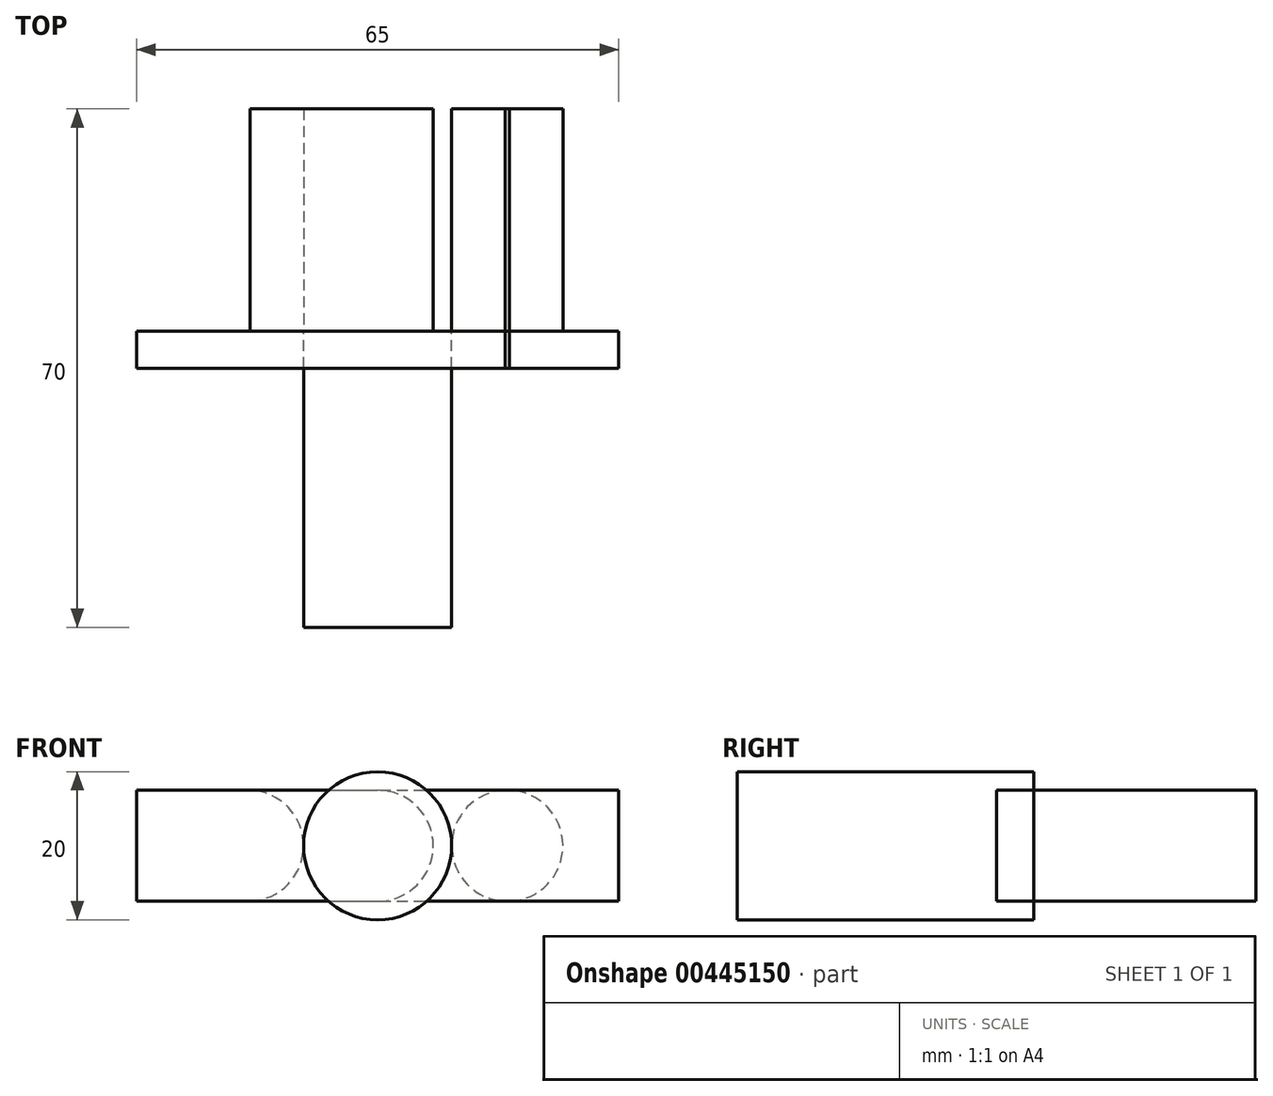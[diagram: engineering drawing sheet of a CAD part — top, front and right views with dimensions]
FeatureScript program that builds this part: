
annotation { "Feature Type Name" : "Feature", "Feature Type Description" : "" }
export const myFeature = defineFeature(function(context is Context, id is Id, definition is map)
    precondition{}
    {
        {
            var Q0;
            Q0=qCreatedBy(makeId("Front.planeOp"),FACE);
            var sketch = newSketch(context, id + "F0", { "sketchPlane" : qUnion([Q0])});
            skLineSegment(sketch, "E0.bottom", {"start": v(-32.5, 7.5) * mm, "end": v(32.5, 7.5) * mm});
            skLineSegment(sketch, "E0.top", {"start": v(-32.5, -7.5) * mm, "end": v(32.5, -7.5) * mm});
            skLineSegment(sketch, "E0.left", {"start": v(-32.5, 7.5) * mm, "end": v(-32.5, -7.5) * mm});
            skLineSegment(sketch, "E0.right", {"start": v(32.5, 7.5) * mm, "end": v(32.5, -7.5) * mm});
            skPoint(sketch, "E0.middle", {"position": v(0, 0) * mm});
            skCircle(sketch, "E1", {"center": v(0, 0) * mm, "radius": 7.5 * mm});
            skCircle(sketch, "E2", {"center": v(-17.5, 0) * mm, "radius": 7.5 * mm});
            skCircle(sketch, "E3", {"center": v(17.5, 0) * mm, "radius": 7.5 * mm});
            skSolve(sketch);
        }
        {
            var Q0;
            {var subQ0=sQuery(id+"F0.wireOp",EDGE,"E0.left");Q0=makeQuery(id+"F0.imprint","IMPRINT",FACE,{"disambiguationData":[TD([[makeQuery(id+"F0.imprint","IMPRINT",EDGE,{"derivedFrom":subQ0}),1.0]])]});}
            var Q1;
            {var subQ0=sQuery(id+"F0.wireOp",EDGE,"E2");var subQ1=sQuery(id+"F0.wireOp",EDGE,"E0.bottom");var subQ2=makeQuery(id+"F0.imprint","INTERSECT",VERTEX,{"disambiguationData":[OD(1.0)],"derivedFrom":[subQ1,subQ0]});Q1=makeQuery(id+"F0.imprint","IMPRINT",FACE,{"disambiguationData":[TD([[makeQuery(id+"F0.imprint","IMPRINT",EDGE,{"disambiguationData":[TD([[subQ2,-1.0]])],"derivedFrom":subQ1}),-1.0]])]});}
            var Q2;
            {var subQ0=sQuery(id+"F0.wireOp",EDGE,"E1");var subQ1=sQuery(id+"F0.wireOp",EDGE,"E0.bottom");var subQ2=makeQuery(id+"F0.imprint","INTERSECT",VERTEX,{"derivedFrom":[subQ1,subQ0]});Q2=makeQuery(id+"F0.imprint","IMPRINT",FACE,{"disambiguationData":[TD([[makeQuery(id+"F0.imprint","IMPRINT",EDGE,{"disambiguationData":[TD([[subQ2,-1.0]])],"derivedFrom":subQ1}),-1.0]])]});}
            var Q3;
            {var subQ0=sQuery(id+"F0.wireOp",EDGE,"E0.right");Q3=makeQuery(id+"F0.imprint","IMPRINT",FACE,{"disambiguationData":[TD([[makeQuery(id+"F0.imprint","IMPRINT",EDGE,{"derivedFrom":subQ0}),-1.0]])]});}
            var Q4;
            {var subQ0=sQuery(id+"F0.wireOp",EDGE,"E3");var subQ1=sQuery(id+"F0.wireOp",EDGE,"E0.top");var subQ2=makeQuery(id+"F0.imprint","INTERSECT",VERTEX,{"disambiguationData":[OD(0.0)],"derivedFrom":[subQ1,subQ0]});Q4=makeQuery(id+"F0.imprint","IMPRINT",FACE,{"disambiguationData":[TD([[makeQuery(id+"F0.imprint","IMPRINT",EDGE,{"disambiguationData":[TD([[subQ2,-1.0]])],"derivedFrom":subQ1}),-1.0]])]});}
            var Q5;
            {var subQ0=sQuery(id+"F0.wireOp",EDGE,"E3");var subQ1=sQuery(id+"F0.wireOp",EDGE,"E0.bottom");var subQ2=makeQuery(id+"F0.imprint","INTERSECT",VERTEX,{"disambiguationData":[OD(0.0)],"derivedFrom":[subQ1,subQ0]});Q5=makeQuery(id+"F0.imprint","IMPRINT",FACE,{"disambiguationData":[TD([[makeQuery(id+"F0.imprint","IMPRINT",EDGE,{"disambiguationData":[TD([[subQ2,-1.0]])],"derivedFrom":subQ1}),1.0]])]});}
            var Q6;
            {var subQ0=sQuery(id+"F0.wireOp",EDGE,"E2");var subQ1=sQuery(id+"F0.wireOp",EDGE,"E0.bottom");var subQ2=makeQuery(id+"F0.imprint","INTERSECT",VERTEX,{"disambiguationData":[OD(0.0)],"derivedFrom":[subQ1,subQ0]});Q6=makeQuery(id+"F0.imprint","IMPRINT",FACE,{"disambiguationData":[TD([[makeQuery(id+"F0.imprint","IMPRINT",EDGE,{"disambiguationData":[TD([[subQ2,-1.0]])],"derivedFrom":subQ1}),1.0]])]});}
            var Q7;
            {var subQ0=sQuery(id+"F0.wireOp",EDGE,"E2");var subQ1=sQuery(id+"F0.wireOp",EDGE,"E0.top");var subQ2=makeQuery(id+"F0.imprint","INTERSECT",VERTEX,{"disambiguationData":[OD(0.0)],"derivedFrom":[subQ1,subQ0]});Q7=makeQuery(id+"F0.imprint","IMPRINT",FACE,{"disambiguationData":[TD([[makeQuery(id+"F0.imprint","IMPRINT",EDGE,{"disambiguationData":[TD([[subQ2,-1.0]])],"derivedFrom":subQ1}),-1.0]])]});}
            var Q8;
            {var subQ0=sQuery(id+"F0.wireOp",EDGE,"E2");var subQ1=sQuery(id+"F0.wireOp",EDGE,"E0.bottom");var subQ2=makeQuery(id+"F0.imprint","INTERSECT",VERTEX,{"disambiguationData":[OD(0.0)],"derivedFrom":[subQ1,subQ0]});Q8=makeQuery(id+"F0.imprint","IMPRINT",FACE,{"disambiguationData":[TD([[makeQuery(id+"F0.imprint","IMPRINT",EDGE,{"disambiguationData":[TD([[subQ2,-1.0]])],"derivedFrom":subQ1}),-1.0]])]});}
            var Q9;
            {var subQ0=sQuery(id+"F0.wireOp",EDGE,"E1");var subQ1=makeQuery(id+"F0.imprint","INTERSECT",VERTEX,{"derivedFrom":[sQuery(id+"F0.wireOp",EDGE,"E0.bottom"),subQ0]});Q9=makeQuery(id+"F0.imprint","IMPRINT",FACE,{"disambiguationData":[TD([[makeQuery(id+"F0.imprint","IMPRINT",EDGE,{"disambiguationData":[TD([[subQ1,-1.0]])],"derivedFrom":subQ0}),1.0]])]});}
            var Q10;
            {var subQ0=sQuery(id+"F0.wireOp",EDGE,"E3");var subQ1=sQuery(id+"F0.wireOp",EDGE,"E0.bottom");var subQ2=makeQuery(id+"F0.imprint","INTERSECT",VERTEX,{"disambiguationData":[OD(0.0)],"derivedFrom":[subQ1,subQ0]});Q10=makeQuery(id+"F0.imprint","IMPRINT",FACE,{"disambiguationData":[TD([[makeQuery(id+"F0.imprint","IMPRINT",EDGE,{"disambiguationData":[TD([[subQ2,-1.0]])],"derivedFrom":subQ1}),-1.0]])]});}
            extrude(context, id + "F1", {"entities" : qUnion([Q0, Q1, Q2, Q3, Q4, Q5, Q6, Q7, Q8, Q9, Q10]), "depth" : 5 * mm});
        }
        {
            var Q0;
            {var subQ0=sQuery(id+"F0.wireOp",EDGE,"E2");var subQ1=sQuery(id+"F0.wireOp",EDGE,"E0.bottom");var subQ2=makeQuery(id+"F0.imprint","INTERSECT",VERTEX,{"disambiguationData":[OD(0.0)],"derivedFrom":[subQ1,subQ0]});Q0=makeQuery(id+"F0.imprint","IMPRINT",FACE,{"disambiguationData":[TD([[makeQuery(id+"F0.imprint","IMPRINT",EDGE,{"disambiguationData":[TD([[subQ2,-1.0]])],"derivedFrom":subQ1}),-1.0]])]});}
            var Q1;
            {var subQ0=sQuery(id+"F0.wireOp",EDGE,"E1");var subQ1=makeQuery(id+"F0.imprint","INTERSECT",VERTEX,{"derivedFrom":[sQuery(id+"F0.wireOp",EDGE,"E0.bottom"),subQ0]});Q1=makeQuery(id+"F0.imprint","IMPRINT",FACE,{"disambiguationData":[TD([[makeQuery(id+"F0.imprint","IMPRINT",EDGE,{"disambiguationData":[TD([[subQ1,-1.0]])],"derivedFrom":subQ0}),1.0]])]});}
            var Q2;
            {var subQ0=sQuery(id+"F0.wireOp",EDGE,"E3");var subQ1=sQuery(id+"F0.wireOp",EDGE,"E0.bottom");var subQ2=makeQuery(id+"F0.imprint","INTERSECT",VERTEX,{"disambiguationData":[OD(0.0)],"derivedFrom":[subQ1,subQ0]});Q2=makeQuery(id+"F0.imprint","IMPRINT",FACE,{"disambiguationData":[TD([[makeQuery(id+"F0.imprint","IMPRINT",EDGE,{"disambiguationData":[TD([[subQ2,-1.0]])],"derivedFrom":subQ1}),-1.0]])]});}
            extrude(context, id + "F2", {"entities" : qUnion([Q0, Q1, Q2]), "oppositeDirection" : true, "depth" : 30 * mm});
        }
        {
            var Q0;
            Q0=qCreatedBy(makeId("Front.planeOp"),FACE);
            var sketch = newSketch(context, id + "F3", { "sketchPlane" : qUnion([Q0])});
            skCircle(sketch, "E4", {"center": v(0, 0) * mm, "radius": 10 * mm});
            skSolve(sketch);
        }
        {
            var Q0;
            Q0 = qSketchRegion(id + "F3", true);
            extrude(context, id + "F4", {"entities" : qUnion([Q0]), "depth" : 40 * mm});
        }
    });
